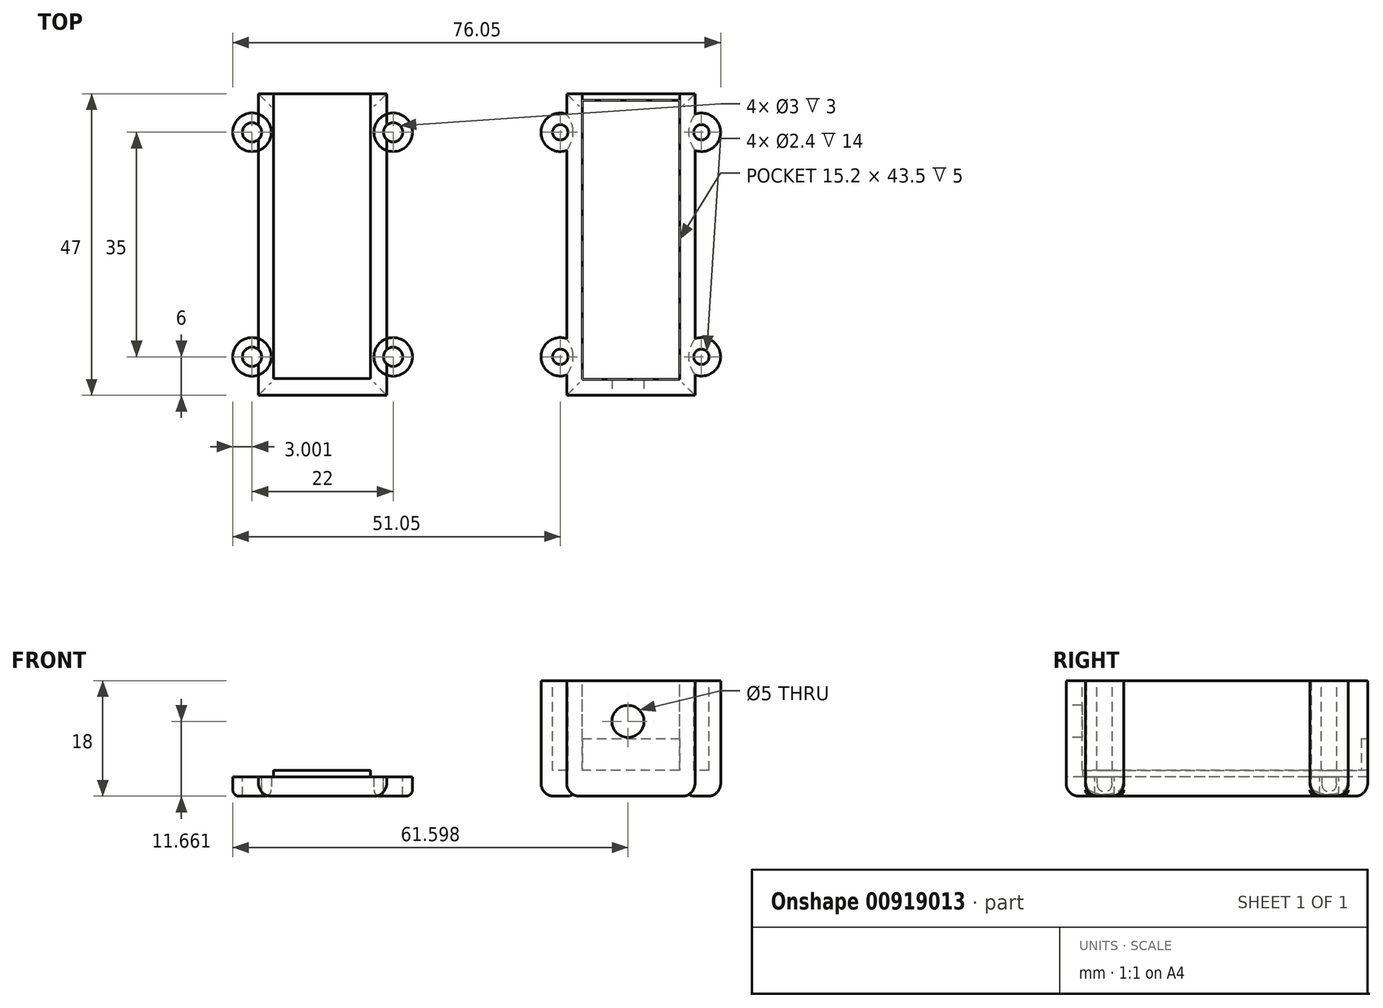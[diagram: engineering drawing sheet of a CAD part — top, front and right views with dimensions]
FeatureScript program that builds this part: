
annotation { "Feature Type Name" : "Feature", "Feature Type Description" : "" }
export const myFeature = defineFeature(function(context is Context, id is Id, definition is map)
    precondition{}
    {
        {
            var Q0;
            Q0=qCreatedBy(makeId("Top.planeOp"),FACE);
            var sketch = newSketch(context, id + "F0", { "sketchPlane" : qUnion([Q0])});
            skLineSegment(sketch, "E0.bottom", {"start": v(-10, 23.5) * mm, "end": v(10, 23.5) * mm});
            skLineSegment(sketch, "E0.top", {"start": v(-10, -23.5) * mm, "end": v(10, -23.5) * mm});
            skLineSegment(sketch, "E0.left", {"start": v(-10, 23.5) * mm, "end": v(-10, -23.5) * mm});
            skLineSegment(sketch, "E0.right", {"start": v(10, 23.5) * mm, "end": v(10, -23.5) * mm});
            skSolve(sketch);
        }
        {
            var Q0;
            Q0=makeQuery(id+"F0.imprint","IMPRINT",FACE,{"disambiguationData":[TD([[makeQuery(id+"F0.imprint","IMPRINT",EDGE,{"derivedFrom":sQuery(id+"F0.wireOp",EDGE,"E0.bottom")}),-1.0]])]});
            extrude(context, id + "F1", {"entities" : qUnion([Q0]), "depth" : 18 * mm, "offsetDistance" : 25 * mm});
        }
        {
            var Q0;
            Q0=makeQuery(id+"F1.opExtrude","CAP_EDGE",EDGE,{"disambiguationData":[OSD([sQuery(id+"F0.wireOp",EDGE,"E0.left")])],"isStart":true});
            var Q1;
            Q1=makeQuery(id+"F1.opExtrude","CAP_EDGE",EDGE,{"disambiguationData":[OSD([sQuery(id+"F0.wireOp",EDGE,"E0.bottom")])],"isStart":true});
            var Q2;
            Q2=makeQuery(id+"F1.opExtrude","CAP_EDGE",EDGE,{"disambiguationData":[OSD([sQuery(id+"F0.wireOp",EDGE,"E0.right")])],"isStart":true});
            var Q3;
            Q3=makeQuery(id+"F1.opExtrude","CAP_EDGE",EDGE,{"disambiguationData":[OSD([sQuery(id+"F0.wireOp",EDGE,"E0.top")])],"isStart":true});
            fillet(context, id + "F2", {"entities" : qUnion([Q0, Q1, Q2, Q3]), "radius" : 2 * mm, "tangentPropagation" : true, "allowEdgeOverflow" : false});
        }
        {
            var Q0;
            Q0=makeQuery(id+"F1.opExtrude","CAP_FACE",FACE,{"disambiguationData":[OSD([sQuery(id+"F0.wireOp",EDGE,"E0.bottom"),sQuery(id+"F0.wireOp",EDGE,"E0.top"),sQuery(id+"F0.wireOp",EDGE,"E0.left"),sQuery(id+"F0.wireOp",EDGE,"E0.right")])],"isStart":false});
            var sketch = newSketch(context, id + "F3", { "sketchPlane" : qUnion([Q0])});
            skLineSegment(sketch, "E1.bottom", {"start": v(7.6, -21) * mm, "end": v(-7.6, -21) * mm});
            skLineSegment(sketch, "E1.top", {"start": v(7.6, 23.5) * mm, "end": v(-7.6, 23.5) * mm});
            skLineSegment(sketch, "E1.left", {"start": v(7.6, -21) * mm, "end": v(7.6, 23.5) * mm});
            skLineSegment(sketch, "E1.right", {"start": v(-7.6, -21) * mm, "end": v(-7.6, 23.5) * mm});
            skSolve(sketch);
        }
        {
            var Q0;
            Q0=makeQuery(id+"F3.imprint","IMPRINT",FACE,{"disambiguationData":[TD([[makeQuery(id+"F3.imprint","IMPRINT",EDGE,{"derivedFrom":sQuery(id+"F3.wireOp",EDGE,"E1.bottom")}),-1.0]])]});
            extrude(context, id + "F4", {"entities" : qUnion([Q0]), "operationType" : NewBodyOperationType.REMOVE, "oppositeDirection" : true, "depth" : 14 * mm, "offsetDistance" : 25 * mm});
        }
        {
            var Q0;
            Q0=makeQuery(id+"F4.boolean.opBoolean","COPY",FACE,{"derivedFrom":makeQuery(id+"F4.opExtrude","CAP_FACE",FACE,{"disambiguationData":[OSD([sQuery(id+"F3.wireOp",EDGE,"E1.bottom"),sQuery(id+"F3.wireOp",EDGE,"E1.top"),sQuery(id+"F3.wireOp",EDGE,"E1.left"),sQuery(id+"F3.wireOp",EDGE,"E1.right")])],"isStart":false})});
            var sketch = newSketch(context, id + "F5", { "sketchPlane" : qUnion([Q0])});
            skCircle(sketch, "E2", {"center": v(0, -16) * mm, "radius": 1.5 * mm});
            skCircle(sketch, "E3", {"center": v(-6.1, 19.5) * mm, "radius": 1.5 * mm});
            skCircle(sketch, "E4", {"center": v(6.1, 19.5) * mm, "radius": 1.5 * mm});
            skSolve(sketch);
        }
        {
            var Q0;
            Q0=sQuery(id+"F5.wireOp",EDGE,"E2");
            var Q1;
            Q1=sQuery(id+"F5.wireOp",EDGE,"E4");
            var Q2;
            Q2=sQuery(id+"F5.wireOp",EDGE,"E3");
            extrude(context, id + "F6", {"bodyType" : ToolBodyType.SURFACE, "surfaceEntities" : qUnion([Q0, Q1, Q2]), "depth" : 3.5 * mm, "offsetDistance" : 25 * mm});
        }
        {
            var Q0;
            Q0=makeQuery(id+"F4.boolean.opBoolean","COPY",FACE,{"derivedFrom":makeQuery(id+"F4.opExtrude","CAP_FACE",FACE,{"disambiguationData":[OSD([sQuery(id+"F3.wireOp",EDGE,"E1.bottom"),sQuery(id+"F3.wireOp",EDGE,"E1.top"),sQuery(id+"F3.wireOp",EDGE,"E1.left"),sQuery(id+"F3.wireOp",EDGE,"E1.right")])],"isStart":false})});
            var sketch = newSketch(context, id + "F7", { "sketchPlane" : qUnion([Q0])});
            skSolve(sketch);
        }
        {
            var Q0;
            Q0=makeQuery(id+"F7.imprint","IMPRINT",FACE,{"disambiguationData":[TD([[makeQuery(id+"F7.imprint","IMPRINT",EDGE,{"derivedFrom":makeQuery(id+"F4.boolean.opBoolean","COPY",EDGE,{"derivedFrom":makeQuery(id+"F4.opExtrude","CAP_EDGE",EDGE,{"disambiguationData":[OSD([sQuery(id+"F3.wireOp",EDGE,"E1.bottom")])],"isStart":false})})}),-1.0]])]});
            var sketch = newSketch(context, id + "F8", { "sketchPlane" : qUnion([Q0])});
            skLineSegment(sketch, "E5.bottom", {"start": v(-7.6, 23.5) * mm, "end": v(7.6, 23.5) * mm});
            skLineSegment(sketch, "E5.top", {"start": v(-7.6, 22.5) * mm, "end": v(7.6, 22.5) * mm});
            skLineSegment(sketch, "E5.left", {"start": v(-7.6, 23.5) * mm, "end": v(-7.6, 22.5) * mm});
            skLineSegment(sketch, "E5.right", {"start": v(7.6, 23.5) * mm, "end": v(7.6, 22.5) * mm});
            skSolve(sketch);
        }
        {
            var Q0;
            Q0=makeQuery(id+"F8.imprint","IMPRINT",FACE,{"disambiguationData":[TD([[makeQuery(id+"F8.imprint","IMPRINT",EDGE,{"derivedFrom":sQuery(id+"F8.wireOp",EDGE,"E5.bottom")}),-1.0]])]});
            extrude(context, id + "F9", {"entities" : qUnion([Q0]), "operationType" : NewBodyOperationType.ADD, "depth" : 5 * mm, "offsetDistance" : 25 * mm});
        }
        {
            var Q0;
            Q0=makeQuery(id+"F1.opExtrude","SWEPT_FACE",FACE,{"disambiguationData":[OSD([sQuery(id+"F0.wireOp",EDGE,"E0.top")])]});
            var sketch = newSketch(context, id + "F10", { "sketchPlane" : qUnion([Q0])});
            skCircle(sketch, "E6", {"center": v(-0.45, 11.66) * mm, "radius": 2.5 * mm});
            skSolve(sketch);
        }
        {
            var Q0;
            Q0=makeQuery(id+"F10.imprint","IMPRINT",FACE,{"disambiguationData":[TD([[makeQuery(id+"F10.imprint","IMPRINT",EDGE,{"derivedFrom":sQuery(id+"F10.wireOp",EDGE,"E6")}),1.0]])]});
            extrude(context, id + "F11", {"entities" : qUnion([Q0]), "operationType" : NewBodyOperationType.REMOVE, "oppositeDirection" : true, "depth" : 10 * mm, "offsetDistance" : 25 * mm});
        }
        {
            var Q0;
            Q0=qCreatedBy(makeId("Top.planeOp"),FACE);
            var sketch = newSketch(context, id + "F12", { "sketchPlane" : qUnion([Q0])});
            skLineSegment(sketch, "E7.bottom", {"start": v(-58.05, 23.5) * mm, "end": v(-38.05, 23.5) * mm});
            skLineSegment(sketch, "E7.top", {"start": v(-58.05, -23.5) * mm, "end": v(-38.05, -23.5) * mm});
            skLineSegment(sketch, "E7.left", {"start": v(-58.05, 23.5) * mm, "end": v(-58.05, -23.5) * mm});
            skLineSegment(sketch, "E7.right", {"start": v(-38.05, 23.5) * mm, "end": v(-38.05, -23.5) * mm});
            skSolve(sketch);
        }
        {
            var Q0;
            Q0 = qSketchRegion(id + "F12", true);
            extrude(context, id + "F13", {"entities" : qUnion([Q0]), "depth" : 3 * mm, "offsetDistance" : 25 * mm});
        }
        {
            var Q0;
            Q0=makeQuery(id+"F13.opExtrude","CAP_FACE",FACE,{"disambiguationData":[OSD([sQuery(id+"F12.wireOp",EDGE,"E7.bottom"),sQuery(id+"F12.wireOp",EDGE,"E7.top"),sQuery(id+"F12.wireOp",EDGE,"E7.left"),sQuery(id+"F12.wireOp",EDGE,"E7.right")])],"isStart":false});
            var sketch = newSketch(context, id + "F14", { "sketchPlane" : qUnion([Q0])});
            skLineSegment(sketch, "E8.bottom", {"start": v(-55.7, 23.5) * mm, "end": v(-40.6, 23.5) * mm});
            skLineSegment(sketch, "E8.top", {"start": v(-55.7, -20.9) * mm, "end": v(-40.6, -20.9) * mm});
            skLineSegment(sketch, "E8.left", {"start": v(-55.7, 23.5) * mm, "end": v(-55.7, -20.9) * mm});
            skLineSegment(sketch, "E8.right", {"start": v(-40.6, 23.5) * mm, "end": v(-40.6, -20.9) * mm});
            skSolve(sketch);
        }
        {
            var Q0;
            Q0 = qSketchRegion(id + "F14", true);
            extrude(context, id + "F15", {"entities" : qUnion([Q0]), "operationType" : NewBodyOperationType.ADD, "depth" : 1 * mm, "offsetDistance" : 25 * mm});
        }
        {
            var Q0;
            Q0=makeQuery(id+"F13.opExtrude","CAP_EDGE",EDGE,{"disambiguationData":[OSD([sQuery(id+"F12.wireOp",EDGE,"E7.right")])],"isStart":true});
            var Q1;
            Q1=makeQuery(id+"F13.opExtrude","CAP_EDGE",EDGE,{"disambiguationData":[OSD([sQuery(id+"F12.wireOp",EDGE,"E7.top")])],"isStart":true});
            var Q2;
            Q2=makeQuery(id+"F13.opExtrude","CAP_EDGE",EDGE,{"disambiguationData":[OSD([sQuery(id+"F12.wireOp",EDGE,"E7.left")])],"isStart":true});
            var Q3;
            Q3=makeQuery(id+"F13.opExtrude","CAP_EDGE",EDGE,{"disambiguationData":[OSD([sQuery(id+"F12.wireOp",EDGE,"E7.bottom")])],"isStart":true});
            fillet(context, id + "F16", {"entities" : qUnion([Q0, Q1, Q2, Q3]), "radius" : 2 * mm, "tangentPropagation" : true, "allowEdgeOverflow" : false});
        }
        {
            var Q0;
            Q0=qCreatedBy(makeId("Top.planeOp"),FACE);
            var Q1;
            Q1=qCreatedBy(makeId("Top.planeOp"),FACE);
            var sketch = newSketch(context, id + "F17", { "sketchPlane" : qUnion([Q0, Q1])});
            skCircle(sketch, "E9", {"center": v(11, 17.5) * mm, "radius": 3 * mm});
            skCircle(sketch, "E10", {"center": v(11, -17.5) * mm, "radius": 3 * mm});
            skCircle(sketch, "E11", {"center": v(-11, 17.5) * mm, "radius": 3 * mm});
            skCircle(sketch, "E12", {"center": v(-11, -17.5) * mm, "radius": 3 * mm});
            skSolve(sketch);
        }
        {
            var Q0;
            Q0=qCreatedBy(makeId("Top.planeOp"),FACE);
            var sketch = newSketch(context, id + "F18", { "sketchPlane" : qUnion([Q0])});
            skCircle(sketch, "E13", {"center": v(-37.05, 17.5) * mm, "radius": 3 * mm});
            skCircle(sketch, "E14", {"center": v(-37.05, -17.5) * mm, "radius": 3 * mm});
            skCircle(sketch, "E15", {"center": v(-59.05, 17.5) * mm, "radius": 3 * mm});
            skCircle(sketch, "E16", {"center": v(-59.05, -17.5) * mm, "radius": 3 * mm});
            skSolve(sketch);
        }
        {
            var Q0;
            Q0 = qSketchRegion(id + "F17", true);
            extrude(context, id + "F19", {"entities" : qUnion([Q0]), "operationType" : NewBodyOperationType.ADD, "depth" : 18 * mm, "offsetDistance" : 25 * mm});
        }
        {
            var Q0;
            Q0 = qSketchRegion(id + "F18", true);
            extrude(context, id + "F20", {"entities" : qUnion([Q0]), "depth" : 3 * mm, "offsetDistance" : 25 * mm});
        }
        {
            var Q0;
            Q0=makeQuery(id+"F19.opExtrude","CAP_EDGE",EDGE,{"disambiguationData":[OSD([sQuery(id+"F17.wireOp",EDGE,"E11")])],"isStart":true});
            var Q1;
            Q1=makeQuery(id+"F19.opExtrude","CAP_EDGE",EDGE,{"disambiguationData":[OSD([sQuery(id+"F17.wireOp",EDGE,"E9")])],"isStart":true});
            var Q2;
            Q2=makeQuery(id+"F19.opExtrude","CAP_EDGE",EDGE,{"disambiguationData":[OSD([sQuery(id+"F17.wireOp",EDGE,"E10")])],"isStart":true});
            var Q3;
            Q3=makeQuery(id+"F19.opExtrude","CAP_EDGE",EDGE,{"disambiguationData":[OSD([sQuery(id+"F17.wireOp",EDGE,"E12")])],"isStart":true});
            fillet(context, id + "F21", {"entities" : qUnion([Q0, Q1, Q2, Q3]), "radius" : 2 * mm, "tangentPropagation" : true, "allowEdgeOverflow" : false});
        }
        {
            var Q0;
            Q0=makeQuery(id+"F20.opExtrude","CAP_EDGE",EDGE,{"disambiguationData":[OSD([sQuery(id+"F18.wireOp",EDGE,"E13")])],"isStart":true});
            var Q1;
            Q1=makeQuery(id+"F20.opExtrude","CAP_EDGE",EDGE,{"disambiguationData":[OSD([sQuery(id+"F18.wireOp",EDGE,"E15")])],"isStart":true});
            var Q2;
            Q2=makeQuery(id+"F20.opExtrude","CAP_EDGE",EDGE,{"disambiguationData":[OSD([sQuery(id+"F18.wireOp",EDGE,"E14")])],"isStart":true});
            var Q3;
            Q3=makeQuery(id+"F20.opExtrude","CAP_EDGE",EDGE,{"disambiguationData":[OSD([sQuery(id+"F18.wireOp",EDGE,"E16")])],"isStart":true});
            fillet(context, id + "F22", {"entities" : qUnion([Q0, Q1, Q2, Q3]), "radius" : 1 * mm, "tangentPropagation" : true, "allowEdgeOverflow" : false});
        }
        {
            var Q0;
            Q0=makeQuery(id+"F20.opExtrude","CAP_FACE",FACE,{"disambiguationData":[OSD([sQuery(id+"F18.wireOp",EDGE,"E13")])],"isStart":false});
            var sketch = newSketch(context, id + "F23", { "sketchPlane" : qUnion([Q0])});
            skCircle(sketch, "E17", {"center": v(-37.05, 17.5) * mm, "radius": 1.5 * mm});
            skCircle(sketch, "E18", {"center": v(-59.05, 17.5) * mm, "radius": 1.5 * mm});
            skCircle(sketch, "E19", {"center": v(-59.05, -17.5) * mm, "radius": 1.5 * mm});
            skCircle(sketch, "E20", {"center": v(-37.05, -17.5) * mm, "radius": 1.5 * mm});
            skSolve(sketch);
        }
        {
            var Q0;
            Q0=makeQuery(id+"F19.boolean.opBoolean","MERGE",FACE,{"derivedFrom":[makeQuery(id+"F1.opExtrude","CAP_FACE",FACE,{"disambiguationData":[OSD([sQuery(id+"F0.wireOp",EDGE,"E0.bottom"),sQuery(id+"F0.wireOp",EDGE,"E0.top"),sQuery(id+"F0.wireOp",EDGE,"E0.left"),sQuery(id+"F0.wireOp",EDGE,"E0.right")])],"isStart":false}),makeQuery(id+"F19.opExtrude","CAP_FACE",FACE,{"disambiguationData":[OSD([sQuery(id+"F17.wireOp",EDGE,"E9")])],"isStart":false}),makeQuery(id+"F19.opExtrude","CAP_FACE",FACE,{"disambiguationData":[OSD([sQuery(id+"F17.wireOp",EDGE,"E10")])],"isStart":false}),makeQuery(id+"F19.opExtrude","CAP_FACE",FACE,{"disambiguationData":[OSD([sQuery(id+"F17.wireOp",EDGE,"E11")])],"isStart":false}),makeQuery(id+"F19.opExtrude","CAP_FACE",FACE,{"disambiguationData":[OSD([sQuery(id+"F17.wireOp",EDGE,"E12")])],"isStart":false})]});
            var sketch = newSketch(context, id + "F24", { "sketchPlane" : qUnion([Q0])});
            skCircle(sketch, "E21", {"center": v(11, 17.5) * mm, "radius": 1.2 * mm});
            skCircle(sketch, "E22", {"center": v(11, -17.5) * mm, "radius": 1.2 * mm});
            skCircle(sketch, "E23", {"center": v(-11, 17.5) * mm, "radius": 1.2 * mm});
            skCircle(sketch, "E24", {"center": v(-11, -17.5) * mm, "radius": 1.2 * mm});
            skSolve(sketch);
        }
        {
            var Q0;
            Q0 = qSketchRegion(id + "F24", true);
            extrude(context, id + "F25", {"entities" : qUnion([Q0]), "operationType" : NewBodyOperationType.REMOVE, "oppositeDirection" : true, "depth" : 14 * mm, "offsetDistance" : 25 * mm});
        }
        {
            var Q0;
            Q0 = qSketchRegion(id + "F23", true);
            extrude(context, id + "F26", {"entities" : qUnion([Q0]), "operationType" : NewBodyOperationType.REMOVE, "oppositeDirection" : true, "depth" : 5 * mm, "offsetDistance" : 25 * mm});
        }
    });
